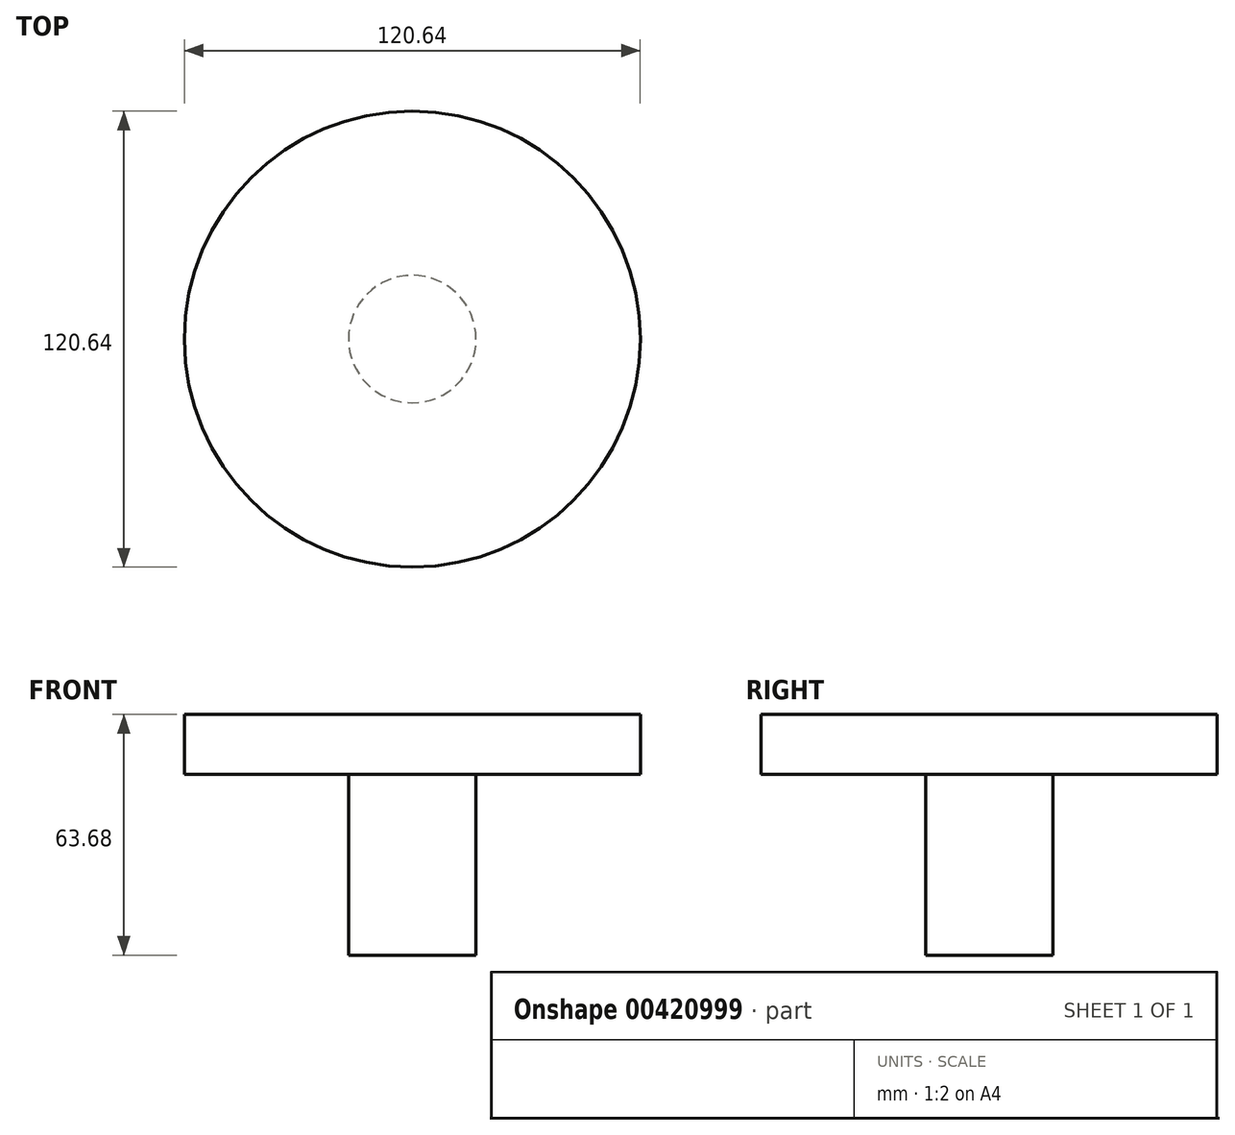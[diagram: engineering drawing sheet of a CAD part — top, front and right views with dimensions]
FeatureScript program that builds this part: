
annotation { "Feature Type Name" : "Feature", "Feature Type Description" : "" }
export const myFeature = defineFeature(function(context is Context, id is Id, definition is map)
    precondition{}
    {
        {
            var Q0;
            Q0=qCreatedBy(makeId("Front.planeOp"),FACE);
            var sketch = newSketch(context, id + "F0", { "sketchPlane" : qUnion([Q0])});
            skLineSegment(sketch, "E0", {"start": v(0, 0) * mm, "end": v(0, 63.68) * mm});
            skLineSegment(sketch, "E1", {"start": v(0, 63.68) * mm, "end": v(60.32, 63.68) * mm});
            skLineSegment(sketch, "E2", {"start": v(60.32, 63.68) * mm, "end": v(60.32, 47.84) * mm});
            skLineSegment(sketch, "E3", {"start": v(60.32, 47.84) * mm, "end": v(16.87, 47.84) * mm});
            skLineSegment(sketch, "E4", {"start": v(16.87, 47.84) * mm, "end": v(16.87, 0) * mm});
            skLineSegment(sketch, "E5", {"start": v(16.87, 0) * mm, "end": v(0, 0) * mm});
            skSolve(sketch);
        }
        {
            var Q0;
            Q0=makeQuery(id+"F0.imprint","IMPRINT",FACE,{"disambiguationData":[TD([[makeQuery(id+"F0.imprint","IMPRINT",EDGE,{"derivedFrom":sQuery(id+"F0.wireOp",EDGE,"E0")}),-1.0]])]});
            var Q1;
            Q1=sQuery(id+"F0.wireOp",EDGE,"E0");
            revolve(context, id + "F1", {"entities" : qUnion([Q0]), "axis" : qUnion([Q1]), "revolveType" : RevolveType.FULL});
        }
    });
